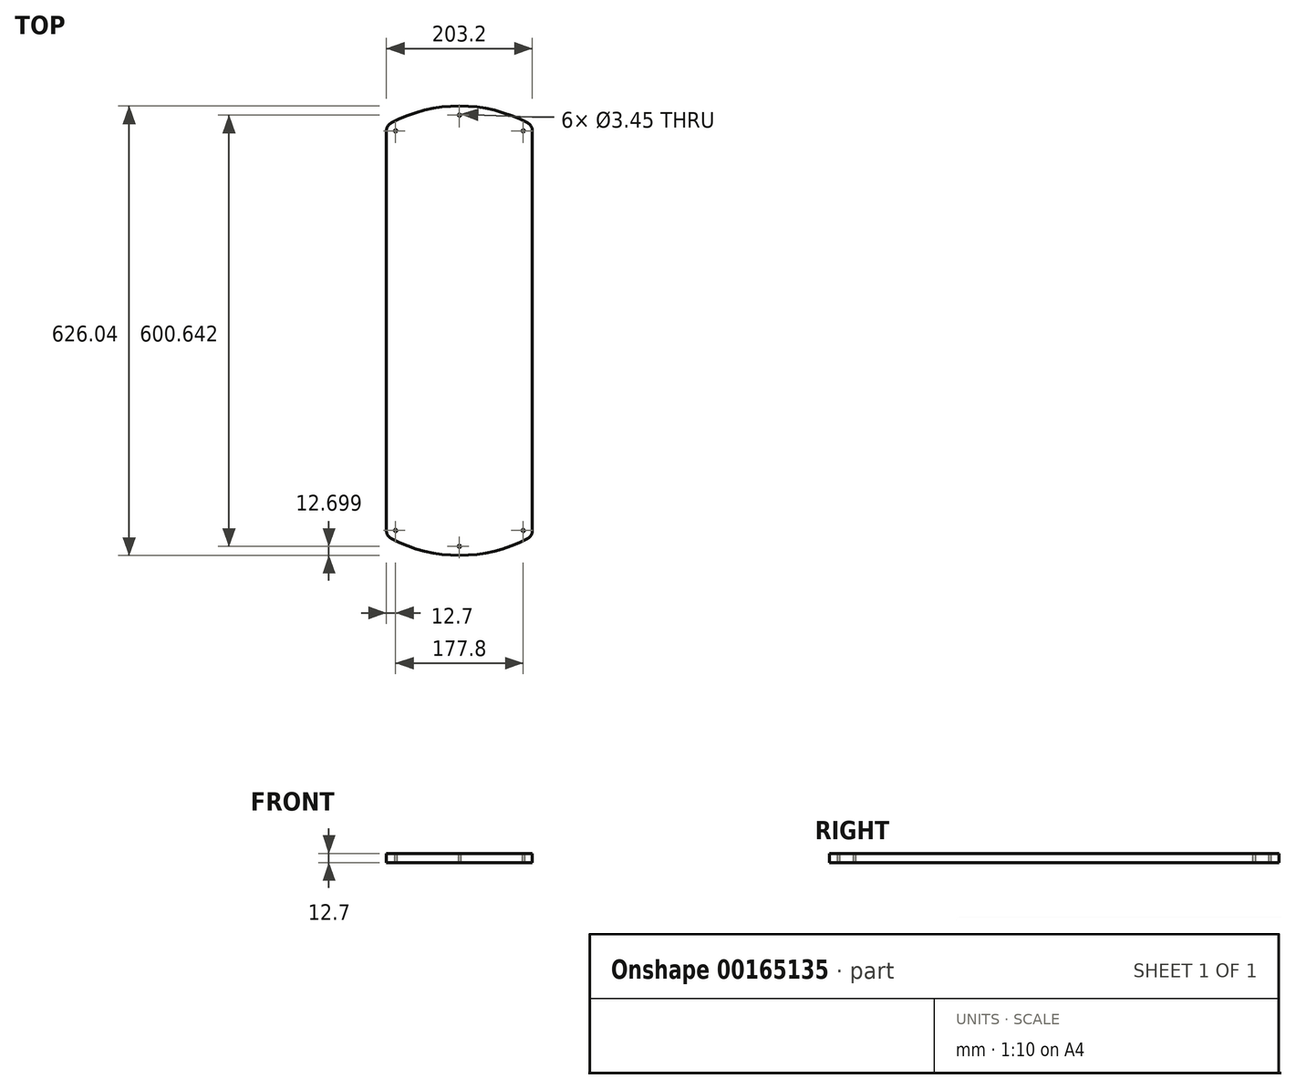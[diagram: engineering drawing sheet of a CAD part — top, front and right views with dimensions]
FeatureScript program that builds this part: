
annotation { "Feature Type Name" : "Feature", "Feature Type Description" : "" }
export const myFeature = defineFeature(function(context is Context, id is Id, definition is map)
    precondition{}
    {
        {
            var Q0;
            Q0=qCreatedBy(makeId("Top.planeOp"),FACE);
            var sketch = newSketch(context, id + "F0", { "sketchPlane" : qUnion([Q0])});
            skLineSegment(sketch, "E0.bottom", {"start": v(101.6, 278.3) * mm, "end": v(-101.6, 278.3) * mm, "construction": true});
            skLineSegment(sketch, "E0.top", {"start": v(101.6, -278.3) * mm, "end": v(-101.6, -278.3) * mm, "construction": true});
            skLineSegment(sketch, "E0.left", {"start": v(101.6, 278.3) * mm, "end": v(101.6, -278.3) * mm});
            skLineSegment(sketch, "E0.right", {"start": v(-101.6, 278.3) * mm, "end": v(-101.6, -278.3) * mm});
            skPoint(sketch, "E0.middle", {"position": v(0, 0) * mm});
            skArc(sketch, "E1", {"start": v(94.83, 289.54) * mm, "mid": v(0, 313.02) * mm, "end": v(-94.83, 289.54) * mm});
            skLineSegment(sketch, "E2", {"start": v(0, 278.3) * mm, "end": v(0, 109.82) * mm, "construction": true});
            skLineSegment(sketch, "E3", {"start": v(0, -109.82) * mm, "end": v(0, -278.3) * mm, "construction": true});
            skLineSegment(sketch, "E4", {"start": v(0, 109.82) * mm, "end": v(44.45, 194.06) * mm, "construction": true});
            skLineSegment(sketch, "E5", {"start": v(-44.45, 194.06) * mm, "end": v(0, 109.82) * mm, "construction": true});
            skLineSegment(sketch, "E6", {"start": v(0, 278.3) * mm, "end": v(0, 300.32) * mm, "construction": true});
            skCircle(sketch, "E7", {"center": v(0, 300.32) * mm, "radius": 12.7 * mm, "construction": true});
            skLineSegment(sketch, "E8", {"start": v(0, 194.06) * mm, "end": v(-44.45, 194.06) * mm, "construction": true});
            skLineSegment(sketch, "E9", {"start": v(0, 194.06) * mm, "end": v(44.45, 194.06) * mm, "construction": true});
            skLineSegment(sketch, "E10", {"start": v(-44.45, 194.06) * mm, "end": v(-88.9, 278.3) * mm, "construction": true});
            skLineSegment(sketch, "E11", {"start": v(44.45, 194.06) * mm, "end": v(88.9, 278.3) * mm, "construction": true});
            skCircle(sketch, "E12", {"center": v(-88.9, 278.3) * mm, "radius": 1.73 * mm});
            skCircle(sketch, "E13", {"center": v(88.9, 278.3) * mm, "radius": 1.73 * mm});
            skCircle(sketch, "E14", {"center": v(0, 300.32) * mm, "radius": 1.73 * mm});
            skArc(sketch, "E15", {"start": v(94.83, -289.54) * mm, "mid": v(99.78, -284.86) * mm, "end": v(101.6, -278.3) * mm});
            skArc(sketch, "E16", {"start": v(-101.6, -278.3) * mm, "mid": v(-99.78, -284.86) * mm, "end": v(-94.83, -289.54) * mm});
            skArc(sketch, "E17", {"start": v(-94.83, -289.54) * mm, "mid": v(0, -313.02) * mm, "end": v(94.83, -289.54) * mm});
            skArc(sketch, "E18", {"start": v(-94.83, 289.54) * mm, "mid": v(-99.78, 284.86) * mm, "end": v(-101.6, 278.3) * mm});
            skArc(sketch, "E19", {"start": v(101.6, 278.3) * mm, "mid": v(99.78, 284.86) * mm, "end": v(94.83, 289.54) * mm});
            skCircle(sketch, "E20", {"center": v(88.9, -278.3) * mm, "radius": 1.73 * mm});
            skCircle(sketch, "E21", {"center": v(-88.9, -278.3) * mm, "radius": 1.73 * mm});
            skLineSegment(sketch, "E22", {"start": v(0, -278.3) * mm, "end": v(0, -300.32) * mm, "construction": true});
            skCircle(sketch, "E23", {"center": v(0, -300.32) * mm, "radius": 12.7 * mm, "construction": true});
            skCircle(sketch, "E24", {"center": v(0, -300.32) * mm, "radius": 1.73 * mm});
            skSolve(sketch);
        }
        {
            var Q0;
            Q0=qSketchRegion(id+"F0",true);
            extrude(context, id + "F1", {"entities" : qUnion([Q0]), "depth" : 12.7 * mm});
        }
    });
